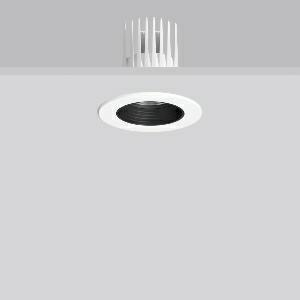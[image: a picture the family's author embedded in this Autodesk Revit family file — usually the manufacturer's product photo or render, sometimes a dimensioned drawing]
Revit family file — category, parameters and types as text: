
# Revit family: heledon_mini_e_901745_002_3_76_464c
name_source: partatom
category: Lighting Fixtures
units: mm (PartAtom-declared; Revit-internal decimal feet)

## family parameters
Cut with Voids When Loaded = No
Host = Face
Light Source = No
Part Type = Normal
Room Calculation Point = No
Round Connector Dimension = Use Diameter
Shared = No

## types (1)
- HELEDON mini E (1 x LED Modul 935, 2000 lm, 3500)
    Apparent Load = 20 VA
    Approval mark = CE
    CIE Flux Codes = 98 100 100 100 100
    Color Rendering = 92
    Color Temperature = 3500
    Default Elevation = 1800 mm
    Description = Series: HELEDON mini
Round recessed downlight. Housing: die-cast aluminium, powder-coated. Black plastic ring and recessed LED to prevent glare from the side. Optical assembly with lens made of plastic (polycarbonate) for the best homogeneous light distribution - can be changed without tools. Best colour rendering index Ra>90. Suitable for Recessed ceiling mounting. Installation without tools thanks to spring fastening system. Including separate LED converter with connecting cable 600 mm.High quality converter without flickering and stroboscopic effect. Through-wiring box (5 pole) available as accessory. The following accessories can be mounted without use of tools: interchangeable lenses, decorative glasses, honeycomb louvre, clear and frosted diffusers, white interchangeable plastic ring. 
Colour: traffic white, matt (RAL 9016)
Diameter: 124 mm
Height: 3 mm
Cut-out diameter: 114 mm
Recess height: 170 mm
Luminaire: recess height: 120 mm
Lamp: LED
Socket: without socket
Colour temperature: 3500K
Colour rendering index (CRI): 92
System power: 20 W
Rated luminous flux: 2000 lm
Luminous efficiency: 100 lm/W
Control gear: Converter, dimmable, DALI
Protection class: II
Type of protection: IP 20
    Height = 0 mm  [stored 0 ft]
    Lamp = 1 x LED Modul 935
    Lamp Light Flux = 2000 lm
    Lamp count = 1
    Length = 124 mm  [stored 0.406824 ft]
    Lifetime = 50000 h
    Luminous efficacy = 100 lm/W
    Manufacturer = RZB
    ModVariant = No
    Model = 901745.002.3.76
    Mounting Place = Ceiling
    Mounting Type = Recessed
    Number of Poles = 1
    OnlyDefault = Yes
    Power Factor = 1
    Product Name = HELEDON mini E
    Product group = Recessed downlights
    ProductGroupID = 402
    Protection Class = Protection class II
    Protection Degree = IP 20
    RLX_Detail_Level = 1
    RLX_Emergency_Light_Flux = 0 lm
    RLX_Emergency_Type = 0
    RLX_Emergency_Type_DB = No
    RlxData = <blob elided: 127617 chars, md5=43a2efec>
    Socket = socket
    Standby Power = 0 W
    System Light Flux = 2000 lm
    System Power = 20 W
    Type Comments = Product without accessories
    Type Image = 901656.002.jpg
    URL = http://relux.com
    VarID = ---
    Voltage = 230 V
    Voltage Range = 220-240 V
    Weight = 0.00 kg
    Width = 0 mm  [stored 0 ft]

note: [stored X ft] marks values corroborated as IEEE doubles in the binary element streams (Revit-internal decimal feet)

## geometry (parser evidence)
native form markers: Blend x4, Sweep x11
no freeform markers — native parametric forms only
